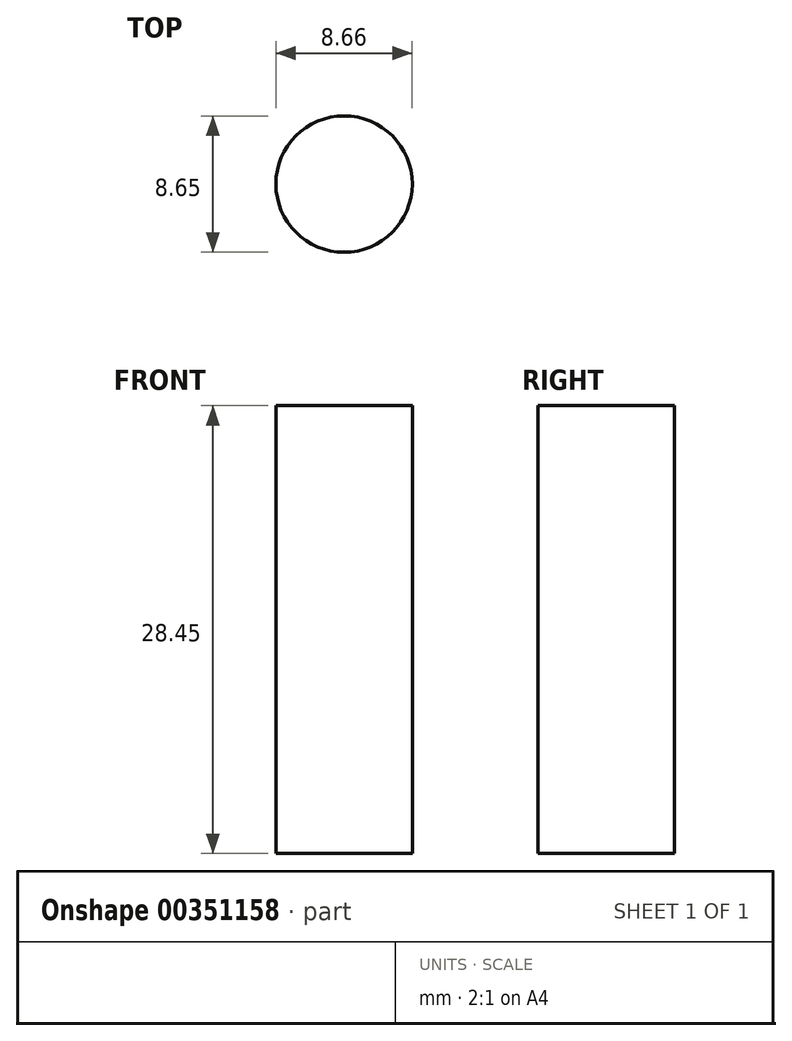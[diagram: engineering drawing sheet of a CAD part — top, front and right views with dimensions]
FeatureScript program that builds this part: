
annotation { "Feature Type Name" : "Feature", "Feature Type Description" : "" }
export const myFeature = defineFeature(function(context is Context, id is Id, definition is map)
    precondition{}
    {
        {
            var Q0;
            Q0=qCreatedBy(makeId("Top.planeOp"),FACE);
            var sketch = newSketch(context, id + "F0", { "sketchPlane" : qUnion([Q0])});
            skCircle(sketch, "E0", {"center": v(-55.19, 27.12) * mm, "radius": 4.33 * mm});
            skSolve(sketch);
        }
        {
            var Q0;
            Q0 = qSketchRegion(id + "F0", true);
            extrude(context, id + "F1", {"entities" : qUnion([Q0]), "depth" : 28.45 * mm});
        }
    });
